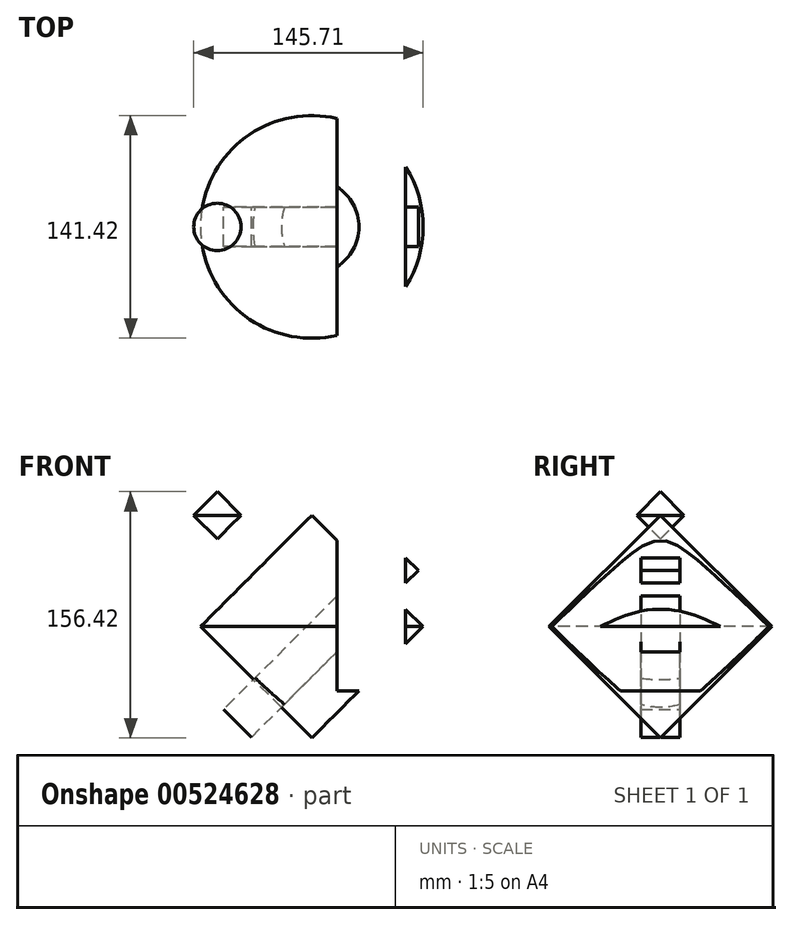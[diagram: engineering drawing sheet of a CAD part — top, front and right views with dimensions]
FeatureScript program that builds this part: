
annotation { "Feature Type Name" : "Feature", "Feature Type Description" : "" }
export const myFeature = defineFeature(function(context is Context, id is Id, definition is map)
    precondition{}
    {
        {
            var Q0;
            Q0=qCreatedBy(makeId("Front.planeOp"),FACE);
            var sketch = newSketch(context, id + "F0", { "sketchPlane" : qUnion([Q0])});
            skLineSegment(sketch, "E0", {"start": v(0, 80.4) * mm, "end": v(0, -82.74) * mm, "construction": true});
            skLineSegment(sketch, "E1", {"start": v(0, 70.71) * mm, "end": v(-70.71, 0) * mm});
            skLineSegment(sketch, "E2", {"start": v(-70.71, 0) * mm, "end": v(0, -70.71) * mm});
            skLineSegment(sketch, "E3", {"start": v(0, -70.71) * mm, "end": v(0, 70.71) * mm});
            skSolve(sketch);
        }
        {
            var Q0;
            Q0=qSketchRegion(id+"F0",true);
            var Q1;
            Q1=sQuery(id+"F0.wireOp",EDGE,"E0");
            revolve(context, id + "F1", {"entities" : qUnion([Q0]), "axis" : qUnion([Q1]), "revolveType" : RevolveType.FULL});
        }
        {
            var Q0;
            Q0=qCreatedBy(makeId("Front.planeOp"),FACE);
            var sketch = newSketch(context, id + "F2", { "sketchPlane" : qUnion([Q0])});
            skLineSegment(sketch, "E4", {"start": v(-45, 70.71) * mm, "end": v(-60, 55.71) * mm});
            skLineSegment(sketch, "E5", {"start": v(-60, 55.71) * mm, "end": v(-60, 85.71) * mm});
            skLineSegment(sketch, "E6", {"start": v(-60, 85.71) * mm, "end": v(-45, 70.71) * mm});
            skLineSegment(sketch, "E7", {"start": v(-60, 47.19) * mm, "end": v(-60, 91.17) * mm, "construction": true});
            skSolve(sketch);
        }
        {
            var Q0;
            Q0=makeQuery(id+"F2.imprint","IMPRINT",FACE,{"disambiguationData":[TD([[makeQuery(id+"F2.imprint","IMPRINT",EDGE,{"derivedFrom":sQuery(id+"F2.wireOp",EDGE,"E4")}),-1.0]])]});
            var Q1;
            Q1=sQuery(id+"F2.wireOp",EDGE,"E7");
            revolve(context, id + "F3", {"entities" : qUnion([Q0]), "axis" : qUnion([Q1]), "revolveType" : RevolveType.FULL});
        }
        {
            var Q0;
            Q0=qCreatedBy(makeId("Front.planeOp"),FACE);
            var sketch = newSketch(context, id + "F4", { "sketchPlane" : qUnion([Q0])});
            skLineSegment(sketch, "E8", {"start": v(50, 53.39) * mm, "end": v(-56.07, -52.68) * mm});
            skLineSegment(sketch, "E9", {"start": v(-56.07, -52.68) * mm, "end": v(-38.39, -70.36) * mm});
            skLineSegment(sketch, "E10", {"start": v(-38.39, -70.36) * mm, "end": v(67.68, 35.71) * mm});
            skLineSegment(sketch, "E11", {"start": v(67.68, 35.71) * mm, "end": v(50, 53.39) * mm});
            skLineSegment(sketch, "E12", {"start": v(-55.42, -15.3) * mm, "end": v(-70.71, 0) * mm});
            skSolve(sketch);
        }
        {
            var Q0;
            Q0=qSketchRegion(id+"F4",true);
            extrude(context, id + "F5", {"entities" : qUnion([Q0]), "endBound" : BoundingType.SYMMETRIC, "depth" : 25 * mm, "offsetDistance" : 25 * mm});
        }
        {
            var Q0;
            Q0=makeQuery(id+"F5.opExtrude","SWEPT_BODY",BODY,{"disambiguationData":[OSD([sQuery(id+"F4.wireOp",EDGE,"E8"),sQuery(id+"F4.wireOp",EDGE,"E9"),sQuery(id+"F4.wireOp",EDGE,"E10"),sQuery(id+"F4.wireOp",EDGE,"E11")])]});
            var Q1;
            Q1=makeQuery(id+"F1.opRevolve","SWEPT_BODY",BODY,{"disambiguationData":[OSD([sQuery(id+"F0.wireOp",EDGE,"E1"),sQuery(id+"F0.wireOp",EDGE,"E2"),sQuery(id+"F0.wireOp",EDGE,"E3")])]});
            booleanBodies(context, id + "F6", {"operationType" : BooleanOperationType.INTERSECTION, "tools" : qUnion([Q0, Q1]), "keepTools" : true});
        }
        {
            var Q0;
            Q0=qCreatedBy(makeId("Front.planeOp"),FACE);
            var sketch = newSketch(context, id + "F7", { "sketchPlane" : qUnion([Q0])});
            skLineSegment(sketch, "E13.bottom", {"start": v(59.64, 67.72) * mm, "end": v(15.97, 67.72) * mm});
            skLineSegment(sketch, "E13.top", {"start": v(59.64, -40.77) * mm, "end": v(15.97, -40.77) * mm});
            skLineSegment(sketch, "E13.left", {"start": v(59.64, 67.72) * mm, "end": v(59.64, -40.77) * mm});
            skLineSegment(sketch, "E13.right", {"start": v(15.97, 67.72) * mm, "end": v(15.97, -40.77) * mm});
            skSolve(sketch);
        }
        {
            var Q0;
            Q0=qSketchRegion(id+"F7",true);
            extrude(context, id + "F8", {"entities" : qUnion([Q0]), "operationType" : NewBodyOperationType.REMOVE, "endBound" : BoundingType.THROUGH_ALL, "oppositeDirection" : true, "depth" : 25 * mm, "offsetDistance" : 25 * mm, "hasSecondDirection" : true, "secondDirectionBound" : SecondDirectionBoundingType.THROUGH_ALL, "secondDirectionOppositeDirection" : false, "secondDirectionDepth" : 25 * mm});
        }
    });
